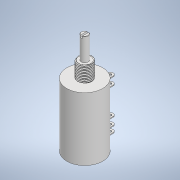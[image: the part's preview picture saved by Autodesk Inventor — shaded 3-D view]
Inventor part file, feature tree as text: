
AUTODESK INVENTOR PART (.ipt)
format: ipt  version: 2022.3 (Build 263350000, 350)  size: 1,267,712 bytes
history: native  units: mm
features: extrude x11, sketch x10, fillet x2, revolve x2, thread x1, helix x1
ambient origin geometry x8: Origin, YZ Plane, XZ Plane, XY Plane, X Axis, Y Axis, Z Axis, Center Point
bodies: Solid1 (feature_tree), Solid2 (feature_tree)
feature tree (27):
  sketch  "Sketch1"  dims[d0=20.5mm d1=5.0mm]
  extrude  "Extrusion1"  Depth=5.0mm
  extrude  "Extrusion2"  Depth=36.0mm TaperAngle=0.0deg
  extrude  "Extrusion3"  Depth=9.0mm TaperAngle=0.0deg
  thread  "Thread1"  [1 undecoded]
  extrude  "Extrusion4"  Depth=9.0mm TaperAngle=0.0deg
  fillet  "Fillet1"  Radius=1.0mm
  extrude  "Extrusion5"  Depth=1.2mm TaperAngle=0.0deg
  extrude  "Extrusion6"  Depth=33.5mm TaperAngle=0.0deg
  sketch  "Sketch5"  dims[d14=4.0mm d15=1.2mm d16=0.0mm]
  extrude  "Extrusion7"  Depth=5.0mm
  extrude  "Extrusion8"  Depth=5.0mm
  sketch  "Sketch6"  dims[d17=0.2mm d18=33.5mm d19=0.0mm]
  extrude  "Extrusion9"  Depth=5.0mm
  extrude  "Extrusion10"  Depth=10.0mm
  extrude  "Extrusion11"  Depth=10.0mm
  fillet  "Fillet2"  Radius=5.0mm
  revolve  "Revolution1"  [1 undecoded]
  revolve  "Revolution2"  [1 undecoded]
  helix  "Coil1"  [1 undecoded]
  sketch  "Sketch2"  dims[d2=2.0mm d3=36.0mm d4=0.0mm]
  sketch  "Sketch3"  dims[d5=8.0mm d6=9.0mm d7=0.0mm d8=4.0mm]
  sketch  "Sketch4"  dims[d9=13.0mm d10=0.0mm d11=9.0mm d12=0.0mm d13=1.0mm]
  sketch  "Sketch7"  dims[d20=2.5mm d21=0.0mm d22=5.0mm]
  sketch  "Sketch8"  dims[d23=0.5mm d24=5.0mm]
  sketch  "Sketch9"  dims[d25=8.0mm d26=5.0mm]
  sketch  "Sketch10"  dims[d27=0.5mm d28=5.0mm d29=5.0mm d30=5.0mm d31=0.5mm d32=5.0mm d33=8.0mm d34=5.0mm d35=5.0mm d36=5.0mm d37=0.5mm d38=5.0mm d39=0.5mm d40=5.0mm d41=0.0mm d42=5.0mm d43=0.0mm d44=1.5mm d45=180.0deg d46=3.0mm d47=1.0mm d48=1.5mm d49=1.5mm d50=10.0mm d51=0.0mm d52=10.0mm d53=0.0mm d54=10.0mm d55=0.75mm d56=0.0mm d57=0.75mm d58=9.599311mm d59=0.120062mm d60=0.120062mm d63=0.75mm d65=9.599311mm d67=0.0mm d68=0.0mm d69=0.75075mm d70=10.5mm d71=10.0mm d72=0.0mm d73=0.0mm d74=0.0mm d75=0.0mm d76=0.0mm]
note: 4 required parameter values undecoded (feature->parameter linkage not recoverable at this tier; creation-order binding heuristic only, values carry confidence <= 0.55)